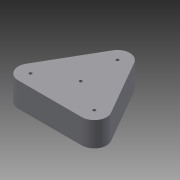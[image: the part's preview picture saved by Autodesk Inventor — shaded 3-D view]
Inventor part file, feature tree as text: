
AUTODESK INVENTOR PART (.ipt)
format: ipt  version: 2013 (Build 170138000, 138)  size: 86,016 bytes
history: native  units: in
note: dims shown in document units (in); Inventor stores cm internally (conversion verified against a paired STEP export)
features: extrude x1, sketch x1
ambient origin geometry x8: Origin, YZ Plane, XZ Plane, XY Plane, X Axis, Y Axis, Z Axis, Center Point
bodies: Solid1 (feature_tree)
feature tree (2):
  extrude  "Extrusion1"  Depth=0.12in
  sketch  "Sketch1"  dims[d1=0.65in d2=0.12in d3=0.03in d4=0.125in d5=0.03in d6=0.25in d7=0.0in]
